# Revit family: FCLLED-non hosted_R16
name_source: partatom
category: Lighting Fixtures
revit_build: Autodesk Revit 2016 (Build: 20150714_1515(x64)
units: mm (PartAtom-declared; Revit-internal decimal feet)

## family parameters
Always vertical = Yes
Cut with Voids When Loaded = No
Light Source = Yes
OmniClass Number = 23.80.70.00
OmniClass Title = Lighting
Part Type = Normal
Room Calculation Point = No
Round Connector Dimension = Use Diameter
Shared = No
Work Plane-Based = No

## types (1)
- FCLLED-non hosted_R16
    Catalogue Number = FCLED
    Color Filter = 16777215
    Construction = Base Material: Polycarbonate
Diffuser Cover Material: Opal Acrylic
    Description = LED CIRCLITE luminiare
    Diffuser = White Opal Acrylic
    Dimensions D x W x H = 348mm (diameter) x 100mm (depth)
    Dimming Lamp Color Temperature Shift = <None>
    IP Rating = IP44
    Lamp = LED Panel Array (30,000hrs), 4000K (default), CRI Ra> 80
    Mounting = Surface Mounted
    Operating Voltage = 240V
    Operating temperature = 1C˚ to 40˚C
    Photometric Web File = 686_240V_Circlite_LED_FCLLED-WW_22062016-01_Revised.ies
    Power Consumption = 16W
    Tilt Angle = 90.00°

## geometry (parser evidence)
native form markers: Sweep x1
no freeform markers — native parametric forms only
